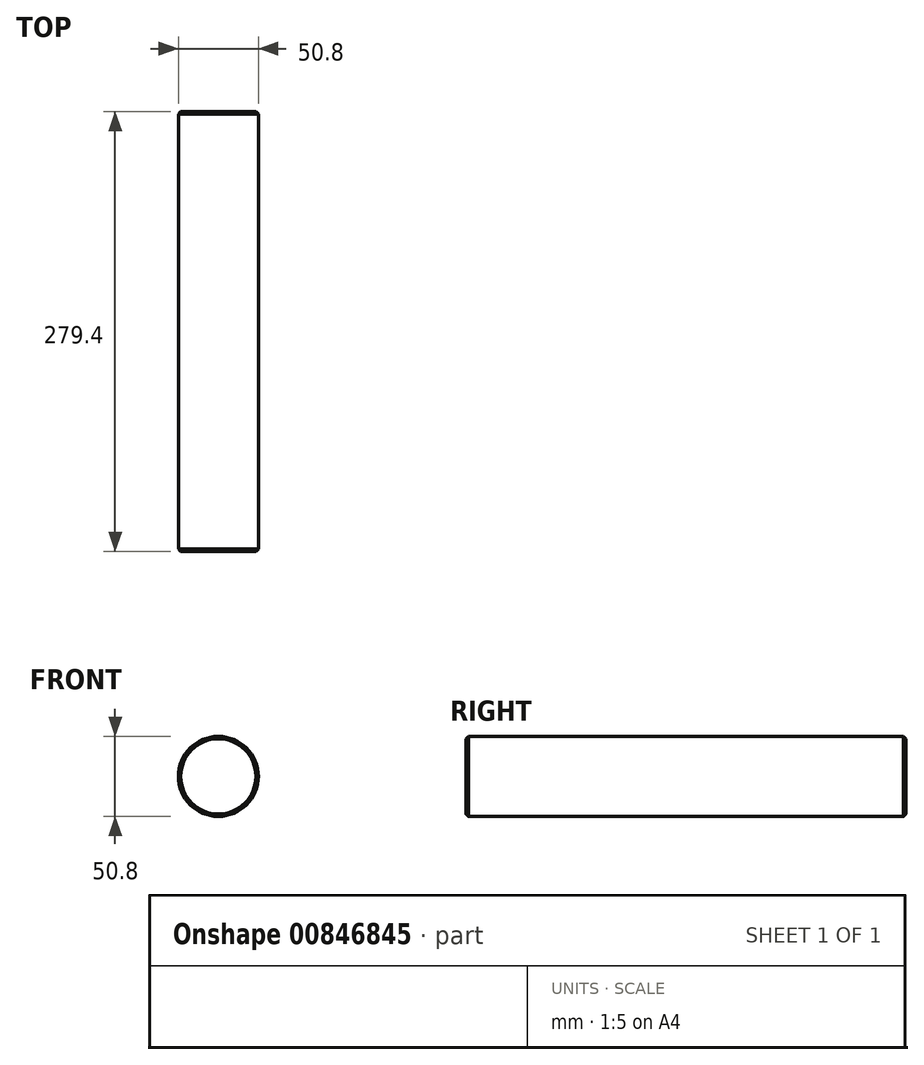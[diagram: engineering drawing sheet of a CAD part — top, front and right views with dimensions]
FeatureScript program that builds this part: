
annotation { "Feature Type Name" : "Feature", "Feature Type Description" : "" }
export const myFeature = defineFeature(function(context is Context, id is Id, definition is map)
    precondition{}
    {
        {
            var Q0;
            Q0=qCreatedBy(makeId("Front.planeOp"),FACE);
            var sketch = newSketch(context, id + "F0", { "sketchPlane" : qUnion([Q0])});
            skCircle(sketch, "E0", {"center": v(0, 0) * mm, "radius": 25.4 * mm});
            skSolve(sketch);
        }
        {
            var Q0;
            Q0 = qSketchRegion(id + "F0", true);
            extrude(context, id + "F1", {"entities" : qUnion([Q0]), "depth" : 279.4 * mm, "offsetDistance" : 25.4 * mm, "symmetric" : true});
        }
        {
            var Q0;
            Q0=makeQuery(id+"F1.opExtrude","SWEPT_FACE",FACE,{"disambiguationData":[OSD([sQuery(id+"F0.wireOp",EDGE,"E0")])]});
            chamfer(context, id + "F2", {"entities" : qUnion([Q0]), "width" : 1.52 * mm, "tangentPropagation" : true});
        }
    });
